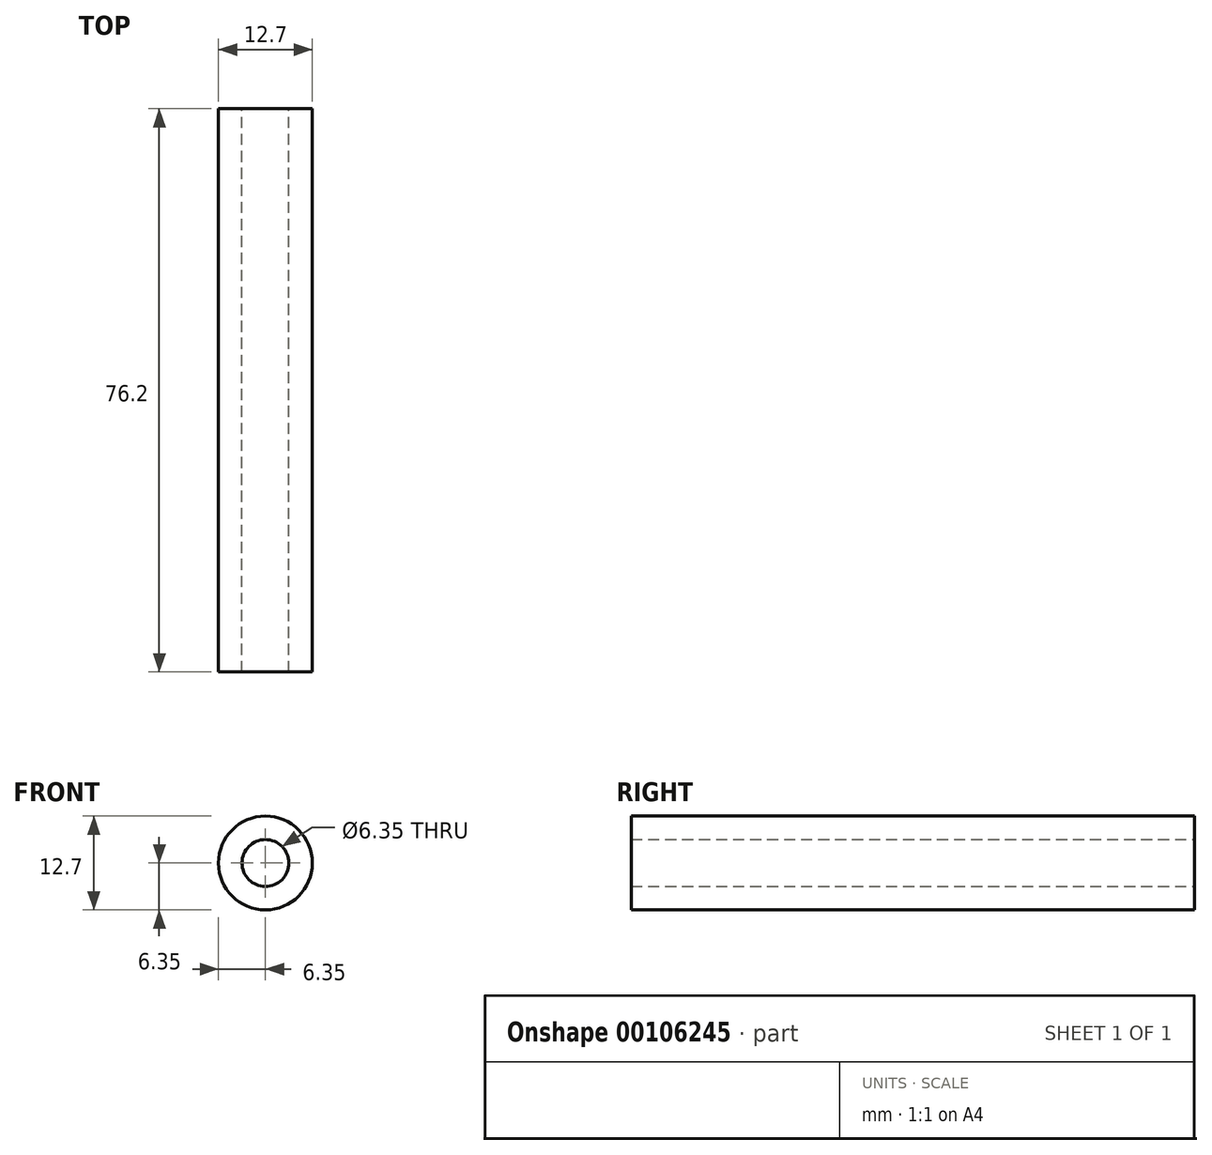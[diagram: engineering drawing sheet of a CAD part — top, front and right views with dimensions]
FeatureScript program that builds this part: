
annotation { "Feature Type Name" : "Feature", "Feature Type Description" : "" }
export const myFeature = defineFeature(function(context is Context, id is Id, definition is map)
    precondition{}
    {
        {
            var Q0;
            Q0=qCreatedBy(makeId("Front.planeOp"),FACE);
            var sketch = newSketch(context, id + "F0", { "sketchPlane" : qUnion([Q0])});
            skCircle(sketch, "E0", {"center": v(0, 0) * mm, "radius": 6.35 * mm});
            skCircle(sketch, "E1", {"center": v(0, 0) * mm, "radius": 3.18 * mm});
            skSolve(sketch);
        }
        {
            var Q0;
            Q0=makeQuery(id+"F0.imprint","IMPRINT",FACE,{"disambiguationData":[TD([[makeQuery(id+"F0.imprint","IMPRINT",EDGE,{"derivedFrom":sQuery(id+"F0.wireOp",EDGE,"E0")}),1.0]])]});
            extrude(context, id + "F1", {"entities" : qUnion([Q0]), "depth" : 76.2 * mm});
        }
    });
